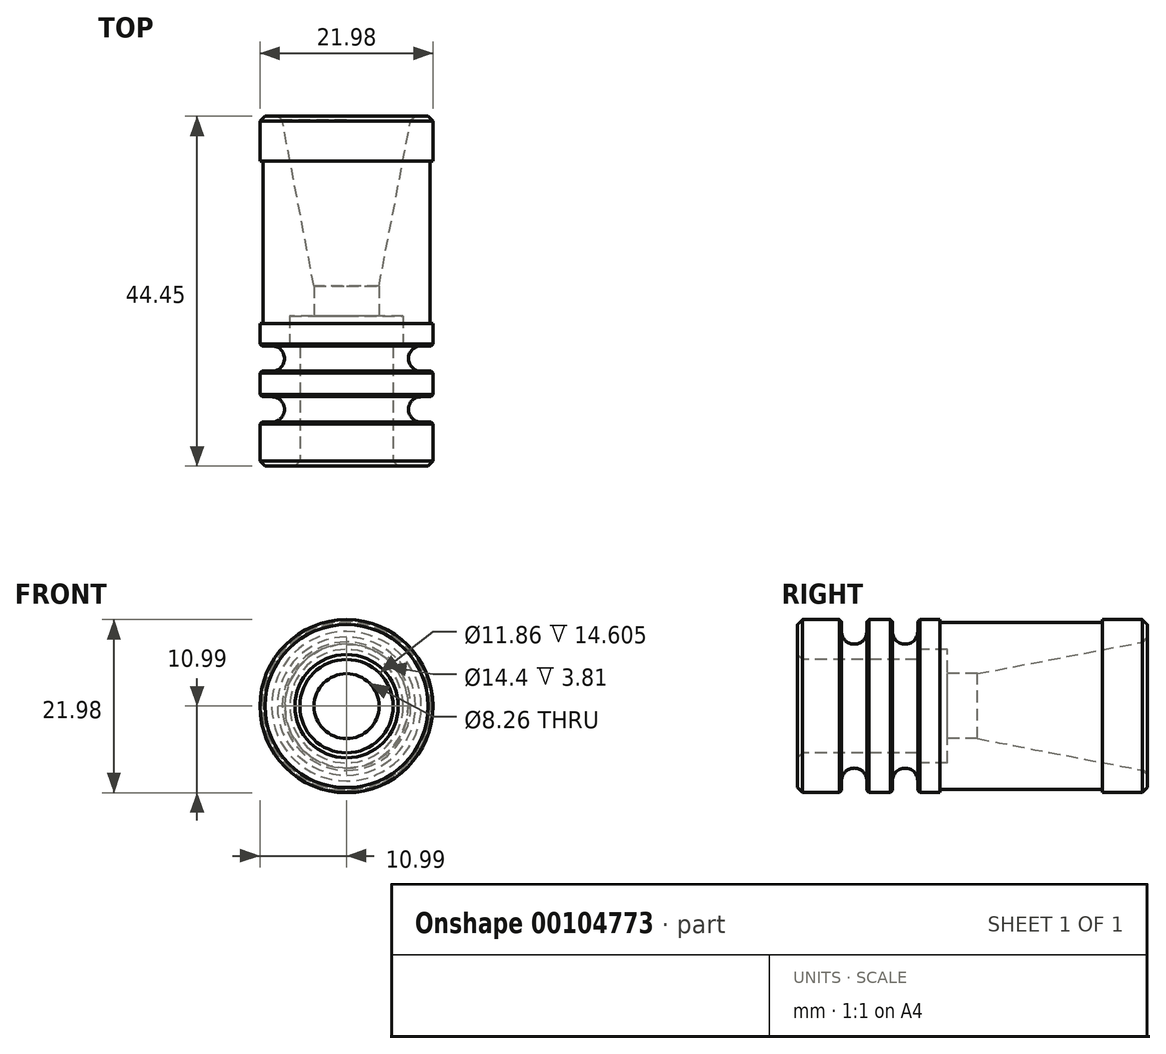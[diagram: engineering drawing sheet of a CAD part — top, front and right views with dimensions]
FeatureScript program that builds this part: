
annotation { "Feature Type Name" : "Feature", "Feature Type Description" : "" }
export const myFeature = defineFeature(function(context is Context, id is Id, definition is map)
    precondition{}
    {
        {
            var Q0;
            Q0=qCreatedBy(makeId("Right.planeOp"),FACE);
            var sketch = newSketch(context, id + "F0", { "sketchPlane" : qUnion([Q0])});
            skLineSegment(sketch, "E0.bottom", {"start": v(22.21, 10.99) * mm, "end": v(16.5, 10.99) * mm});
            skLineSegment(sketch, "E0.left", {"start": v(22.21, 10.99) * mm, "end": v(22.21, 8.26) * mm});
            skLineSegment(sketch, "E0.right", {"start": v(-22.24, 10.99) * mm, "end": v(-22.24, 4.13) * mm});
            skPoint(sketch, "E0.middle", {"position": v(0, 0) * mm});
            skLineSegment(sketch, "E1", {"start": v(-16.65, 10.99) * mm, "end": v(-16.65, 9.5) * mm});
            skLineSegment(sketch, "E2", {"start": v(-10.18, 10.99) * mm, "end": v(-10.18, 9.49) * mm});
            skLineSegment(sketch, "E3", {"start": v(-6.96, 10.99) * mm, "end": v(-6.96, 9.49) * mm});
            skLineSegment(sketch, "E4", {"start": v(16.5, 10.99) * mm, "end": v(16.5, 10.85) * mm});
            skLineSegment(sketch, "E5.bottom", {"start": v(-15.02, 7.87) * mm, "end": v(-15.02, 7.87) * mm});
            skLineSegment(sketch, "E6.trimOffspring", {"start": v(-16.65, 10.99) * mm, "end": v(-22.24, 10.99) * mm});
            skLineSegment(sketch, "E7.trimOffspring", {"start": v(-10.18, 10.99) * mm, "end": v(-13.42, 10.99) * mm});
            skLineSegment(sketch, "E8.trimOffspring", {"start": v(-8.57, 7.87) * mm, "end": v(-8.57, 7.87) * mm});
            skArc(sketch, "E9.filletArc", {"start": v(-10.18, 9.49) * mm, "mid": v(-9.71, 8.35) * mm, "end": v(-8.57, 7.87) * mm});
            skArc(sketch, "E10.filletArc", {"start": v(-8.57, 7.87) * mm, "mid": v(-7.43, 8.35) * mm, "end": v(-6.96, 9.49) * mm});
            skLineSegment(sketch, "E11", {"start": v(-4.15, 10.99) * mm, "end": v(-4.15, 10.85) * mm});
            skLineSegment(sketch, "E12", {"start": v(-3.9, 10.6) * mm, "end": v(16.25, 10.6) * mm});
            skLineSegment(sketch, "E13.trimOffspring", {"start": v(-4.15, 10.99) * mm, "end": v(-6.96, 10.99) * mm});
            skArc(sketch, "E14.filletArc", {"start": v(16.25, 10.6) * mm, "mid": v(16.43, 10.68) * mm, "end": v(16.5, 10.85) * mm});
            skArc(sketch, "E15.filletArc", {"start": v(-4.15, 10.85) * mm, "mid": v(-4.08, 10.68) * mm, "end": v(-3.9, 10.6) * mm});
            skPoint(sketch, "E16", {"position": v(0.62, 4.13) * mm});
            skLineSegment(sketch, "E17", {"start": v(22.21, 8.26) * mm, "end": v(0.62, 4.13) * mm});
            skLineSegment(sketch, "E18", {"start": v(0.62, 4.13) * mm, "end": v(-3.19, 4.13) * mm});
            skLineSegment(sketch, "E19", {"start": v(-22.24, 4.13) * mm, "end": v(-22.24, 0) * mm});
            skLineSegment(sketch, "E20", {"start": v(22.21, 8.26) * mm, "end": v(22.21, 0) * mm});
            skLineSegment(sketch, "E21", {"start": v(-22.24, 0) * mm, "end": v(22.21, 0) * mm});
            skArc(sketch, "E22", {"start": v(-16.65, 9.5) * mm, "mid": v(-16.17, 8.35) * mm, "end": v(-15.02, 7.87) * mm});
            skLineSegment(sketch, "E23", {"start": v(-13.42, 10.99) * mm, "end": v(-13.42, 9.5) * mm});
            skArc(sketch, "E24", {"start": v(-15.02, 7.87) * mm, "mid": v(-13.88, 8.35) * mm, "end": v(-13.42, 9.5) * mm});
            skLineSegment(sketch, "E25", {"start": v(-3.19, 4.13) * mm, "end": v(-3.19, 5.93) * mm});
            skLineSegment(sketch, "E26", {"start": v(-22.24, 5.93) * mm, "end": v(-7, 5.93) * mm});
            skLineSegment(sketch, "E27", {"start": v(-3.19, 5.93) * mm, "end": v(-3.19, 7.2) * mm});
            skLineSegment(sketch, "E28", {"start": v(-7, 5.93) * mm, "end": v(-7, 7.2) * mm});
            skLineSegment(sketch, "E29", {"start": v(-7, 7.2) * mm, "end": v(-3.19, 7.2) * mm});
            skSolve(sketch);
        }
        {
            var Q0;
            Q0=makeQuery(id+"F0.imprint","IMPRINT",FACE,{"disambiguationData":[TD([[makeQuery(id+"F0.imprint","IMPRINT",EDGE,{"derivedFrom":sQuery(id+"F0.wireOp",EDGE,"E0.bottom")}),1.0]])]});
            var Q1;
            Q1=sQuery(id+"F0.wireOp",EDGE,"E21");
            revolve(context, id + "F1", {"entities" : qUnion([Q0]), "axis" : qUnion([Q1]), "revolveType" : RevolveType.FULL});
        }
        {
            var Q0;
            Q0=makeQuery(id+"F1.opRevolve","SWEPT_FACE",FACE,{"disambiguationData":[OSD([sQuery(id+"F0.wireOp",EDGE,"E0.left")])]});
            chamfer(context, id + "F2", {"entities" : qUnion([Q0]), "width" : 0.64 * mm, "tangentPropagation" : true});
        }
        {
            var Q0;
            Q0=makeQuery(id+"F1.opRevolve","SWEPT_FACE",FACE,{"disambiguationData":[OSD([sQuery(id+"F0.wireOp",EDGE,"E0.right")])]});
            chamfer(context, id + "F3", {"entities" : qUnion([Q0]), "width" : 0.64 * mm, "tangentPropagation" : true});
        }
        {
            var Q0;
            Q0=makeQuery(id+"F1.opRevolve","SWEPT_EDGE",EDGE,{"disambiguationData":[OSD([sQuery(id+"F0.wireOp",EDGE,"E3"),sQuery(id+"F0.wireOp",EDGE,"E13.trimOffspring")])]});
            var Q1;
            Q1=makeQuery(id+"F1.opRevolve","SWEPT_EDGE",EDGE,{"disambiguationData":[OSD([sQuery(id+"F0.wireOp",EDGE,"E7.trimOffspring"),sQuery(id+"F0.wireOp",EDGE,"E23")])]});
            var Q2;
            Q2=makeQuery(id+"F1.opRevolve","SWEPT_EDGE",EDGE,{"disambiguationData":[OSD([sQuery(id+"F0.wireOp",EDGE,"E1"),sQuery(id+"F0.wireOp",EDGE,"E6.trimOffspring")])]});
            var Q3;
            Q3=makeQuery(id+"F1.opRevolve","SWEPT_EDGE",EDGE,{"disambiguationData":[OSD([sQuery(id+"F0.wireOp",EDGE,"E2"),sQuery(id+"F0.wireOp",EDGE,"E7.trimOffspring")])]});
            chamfer(context, id + "F4", {"entities" : qUnion([Q0, Q1, Q2, Q3]), "width" : 0.25 * mm, "tangentPropagation" : true});
        }
    });
